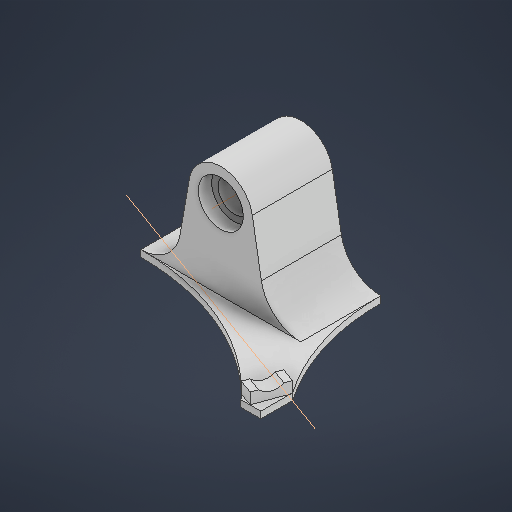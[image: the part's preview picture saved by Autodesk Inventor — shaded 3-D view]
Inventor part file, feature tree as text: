
AUTODESK INVENTOR PART (.ipt)
format: ipt  version: 2025.3 (Build 293356030, 356C)  size: 289,280 bytes
history: native  units: mm
features: extrude x7, sketch x4, other x2, plane x2, projected_geometry x1
ambient origin geometry x8: Origin, YZ Plane, XZ Plane, XY Plane, X Axis, Y Axis, Z Axis, Center Point
bodies: Body1 (feature_tree)
feature tree (16):
  sketch  "Sketch1"  dims[d2=16.9mm d3=12.0mm]
  extrude  "Extrusion3"  Depth=12.0mm
  extrude  "Extrusion4"  Depth=12.0mm
  other  "Work Axis1"
  extrude  "Extrusion5"  Depth=60.0mm
  extrude  "Extrusion6"  Depth=30.0mm TaperAngle=0.0deg
  plane  "Work Plane1"
  plane  "Work Plane3"
  extrude  "Extrusion9"  Depth=20.0mm TaperAngle=0.0deg
  other  "Work Axis3"
  extrude  "Extrusion10"  Depth=15.0mm TaperAngle=0.0deg
  extrude  "Extrusion11"  Depth=15.0mm TaperAngle=0.0deg
  sketch  "Sketch5"  dims[d9=30.0mm d12=12.0mm]
  sketch  "Sketch6"  dims[d15=15.0mm d16=60.0mm]
  projected_geometry  "Projected Loop1"
  sketch  "Sketch7"  dims[d17=2.5mm d18=30.0mm d19=0.0mm d20=20.0mm d21=0.0mm d22=15.0mm d23=0.0mm d24=45.0mm d25=0.0mm d26=12.217305mm d45=7.5mm d46=12.0mm d47=10.7mm d48=14.6mm d49=8.0mm d51=1.5mm d52=5.5mm d53=0.0mm d54=15.0mm d55=0.0mm d56=0.0mm d57=0.0mm d30=0.5mm d31=0.872665mm d32=0.5mm d33=0.872665mm]
